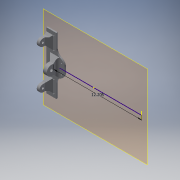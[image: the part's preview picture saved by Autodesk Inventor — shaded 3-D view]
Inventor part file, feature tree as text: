
AUTODESK INVENTOR PART (.ipt)
format: ipt  version: 2016 (Build 200138000, 138)  size: 280,576 bytes
history: native  units: in
note: dims shown in document units (in); Inventor stores cm internally (conversion verified against a paired STEP export)
features: reference x12, sketch x8, projected_geometry x8, extrude x7, chamfer x5, plane x2, fillet x2
ambient origin geometry x8: Origin, YZ Plane, XZ Plane, XY Plane, X Axis, Y Axis, Z Axis, Center Point
bodies: Solid1 (feature_tree)
feature tree (44):
  plane  "Work Plane1"
  extrude  "Extrusion1"  Depth=1.0in
  fillet  "Fillet1"  Radius=12.2047in
  sketch  "Sketch2"  dims[d4=0.0in d5=0.0in d6=0.4in d7=0.0in]
  plane  "Work Plane2"
  extrude  "Extrusion2"  Depth=0.4in TaperAngle=0.0deg
  extrude  "Extrusion3"  Depth=0.3937in
  chamfer  "Chamfer1"  Distance=0.2in
  extrude  "Extrusion4"  Depth=1.0in TaperAngle=45.0deg
  fillet  "Fillet2"  Radius=1.8625in
  chamfer  "Chamfer2"  Distance=1.0in
  extrude  "Extrusion5"  Depth=0.5625in TaperAngle=45.0deg
  extrude  "Extrusion6"  Depth=1.0in TaperAngle=0.0deg
  chamfer  "Chamfer3"  [1 undecoded]
  chamfer  "Chamfer4"  [1 undecoded]
  chamfer  "Chamfer5"  [1 undecoded]
  extrude  "Extrusion7"  [1 undecoded]
  sketch  "Sketch1"  dims[d0=0.2in d1=0.0in d2=1.0in d3=12.2047in]
  reference  "Reference1"
  reference  "Reference2"
  reference  "Reference3"
  reference  "Reference4"
  reference  "Reference5"
  reference  "Reference6"
  reference  "Reference7"
  reference  "Reference8"
  sketch  "Sketch3"  dims[d8=0.5625in d9=0.125in d10=45.0deg d11=0.3937in d12=0.2in d13=0.0in]
  reference  "Reference9"
  reference  "Reference10"
  reference  "Reference11"
  sketch  "Sketch4"  dims[d14=0.375in d15=0.5625in d16=0.125in d17=45.0deg d18=1.8625in d19=0.0in d20=1.0in d21=0.0in]
  projected_geometry  "Projected Loop1"
  projected_geometry  "Projected Loop2"
  sketch  "Sketch5"  dims[d22=0.5625in d23=0.125in d24=45.0deg d25=0.5625in d26=0.125in d27=45.0deg]
  projected_geometry  "Projected Loop3"
  sketch  "Sketch6"  dims[d28=0.25in d29=0.125in d30=45.0deg d31=1.0in d32=0.0in]
  projected_geometry  "Projected Loop4"
  projected_geometry  "Projected Loop5"
  projected_geometry  "Projected Loop6"
  projected_geometry  "Projected Loop7"
  sketch  "Sketch7"
  projected_geometry  "Projected Loop8"
  sketch  "Sketch8"
  reference  "Reference12"
note: 4 required parameter values undecoded (feature->parameter linkage not recoverable at this tier; creation-order binding heuristic only, values carry confidence <= 0.55)
